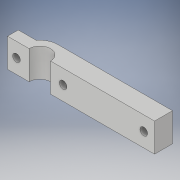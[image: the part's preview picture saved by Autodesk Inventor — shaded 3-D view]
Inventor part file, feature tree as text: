
AUTODESK INVENTOR PART (.ipt)
format: ipt  version: 2017 SP1 (Build 210196100, 196)  size: 131,072 bytes
history: native  units: in
note: dims shown in document units (in); Inventor stores cm internally (conversion verified against a paired STEP export)
features: hole x4, sketch x3, extrude x1
ambient origin geometry x8: Origin, YZ Plane, XZ Plane, XY Plane, X Axis, Y Axis, Z Axis, Center Point
bodies: Solid1 (feature_tree)
feature tree (8):
  extrude  "Extrusion1"  Depth=0.75in
  hole  "Hole1"  [1 undecoded]
  hole  "Hole2"  [1 undecoded]
  hole  "Hole4"  [1 undecoded]
  sketch  "Sketch2"  dims[d0=3.0in d1=0.75in]
  sketch  "Sketch3"  dims[d2=1.25in d3=0.5in]
  sketch  "Sketch4"  dims[d4=0.375in d5=4.0in d6=1.0in d7=0.0in d8=0.266in d9=0.75in d10=0.507in d11=0.25in d12=0.5635in d13=1.0in d14=0.8108in d15=0.375in d16=0.266in d17=0.75in d18=0.507in d19=0.25in d20=0.5635in d21=1.0in d22=0.8108in d23=0.266in d24=0.75in d25=0.375in d26=0.25in d27=0.5635in d28=1.0in d29=0.0in]
  hole  "Hole3"  [1 undecoded]
note: 4 required parameter values undecoded (feature->parameter linkage not recoverable at this tier; creation-order binding heuristic only, values carry confidence <= 0.55)
